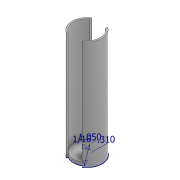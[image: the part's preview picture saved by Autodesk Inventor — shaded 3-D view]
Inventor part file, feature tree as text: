
AUTODESK INVENTOR PART (.ipt)
format: ipt  version: 2020.4 (Build 244396000, 396)  size: 98,304 bytes
history: native  units: in
note: dims shown in document units (in); Inventor stores cm internally (conversion verified against a paired STEP export)
features: extrude x2, sketch x1
ambient origin geometry x8: Origin, YZ Plane, XZ Plane, XY Plane, X Axis, Y Axis, Z Axis, Center Point
bodies: Solid1 (feature_tree)
feature tree (3):
  sketch  "Sketch1"  dims[d0=1.05in d1=0.0625in d6=0.31in d7=4.25in d8=0.0in d9=0.125in d10=0.0in d11=0.0625in]
  extrude  "Extrusion1"  Depth=0.125in
  extrude  "Extrusion2"  Depth=0.125in
